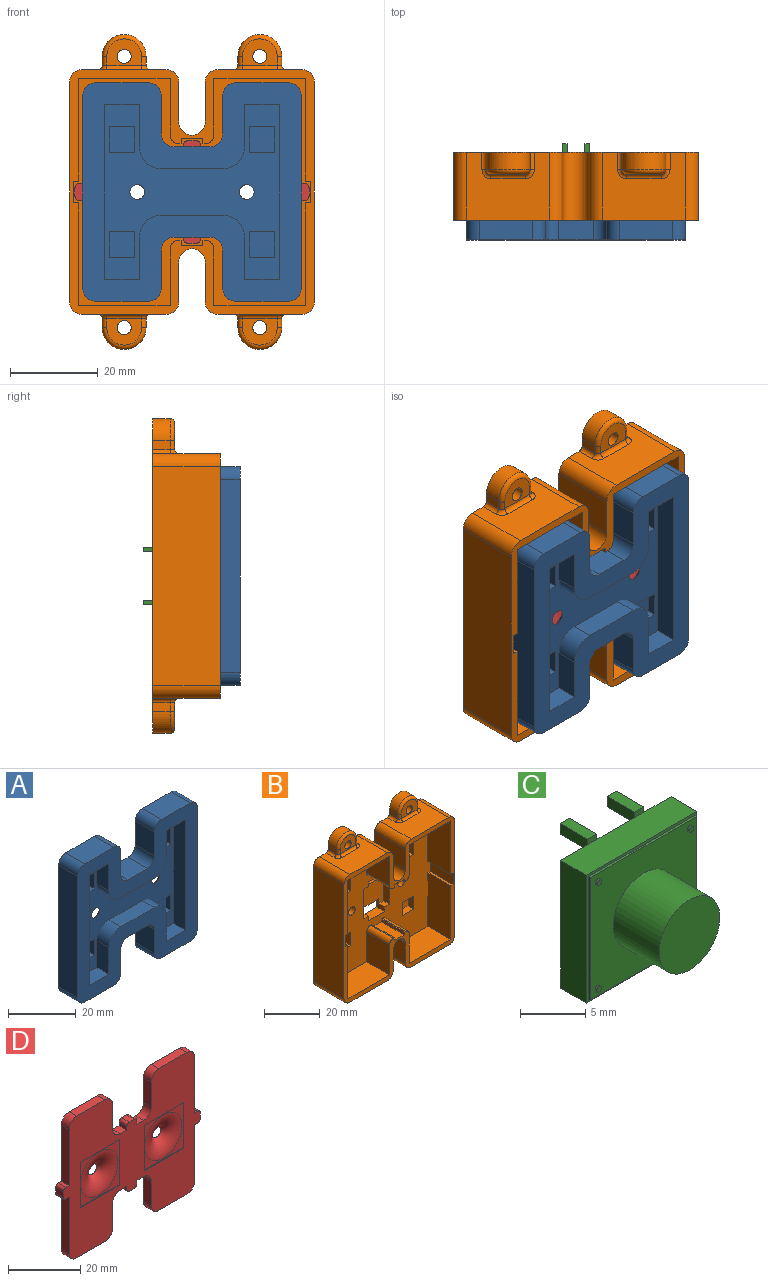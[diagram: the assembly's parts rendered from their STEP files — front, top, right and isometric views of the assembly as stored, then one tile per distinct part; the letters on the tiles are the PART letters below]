
ASSEMBLY  parts=4 mates=3
PART A: 75 faces, bbox 50x8x50 mm
  f0: plane 40x40mm, normal (0,-1,0), area 763.1mm2, adj f14,f15,f16,f17,f18,f19,f20,f21
  f1: plane 50x50mm, normal (0,1,0), area 1606.4mm2, adj f2,f3,f4,f5,f6,f7,f8,f9
  f2: plane 8x8mm, normal (0,0,-1), area 64mm2, adj f1,f26,f32,f33
  f3: plane 8.7x8mm, normal (-1,0,0), area 69.6mm2, adj f1,f26,f33,f34
  f4: plane 12x8mm, normal (0,0,-1), area 96mm2, adj f1,f26,f34,f35
  f5: plane 44x8mm, normal (1,0,0), area 352mm2, adj f1,f26,f35,f36
  f6: plane 12x8mm, normal (0,0,1), area 96mm2, adj f1,f26,f36,f37
  f7: plane 8.7x8mm, normal (-1,0,0), area 69.6mm2, adj f1,f26,f37,f38
  f8: plane 8x8mm, normal (0,0,1), area 64mm2, adj f1,f26,f27,f38
  f9: plane 8.7x8mm, normal (1,0,0), area 69.6mm2, adj f1,f26,f27,f28
  f10: plane 12x8mm, normal (0,0,1), area 96mm2, adj f1,f26,f28,f29
  f11: plane 44x8mm, normal (-1,0,0), area 352mm2, adj f1,f26,f29,f30
  f12: plane 12x8mm, normal (0,0,-1), area 96mm2, adj f1,f26,f30,f31
  f13: plane 8.7x8mm, normal (1,0,0), area 69.6mm2, adj f1,f26,f31,f32
  f14: plane 40x5mm, normal (1,0,0), area 200mm2, adj f0,f15,f25,f26
  f15: plane 8x5mm, normal (0,0,-1), area 40mm2, adj f0,f14,f16,f26
  f16: plane 9.7x5mm, normal (-1,0,0), area 48.5mm2, adj f0,f15,f26,f49
  f17: plane 14x5mm, normal (0,0,-1), area 70mm2, adj f0,f26,f49,f50
  f18: plane 9.7x5mm, normal (1,0,0), area 48.5mm2, adj f0,f19,f26,f50
  f19: plane 8x5mm, normal (0,0,-1), area 40mm2, adj f0,f18,f20,f26
  f20: plane 40x5mm, normal (-1,0,0), area 200mm2, adj f0,f19,f21,f26
  f21: plane 8x5mm, normal (0,0,1), area 40mm2, adj f0,f20,f22,f26
  f22: plane 9.7x5mm, normal (1,0,0), area 48.5mm2, adj f0,f21,f26,f51
  f23: plane 14x5mm, normal (0,0,1), area 70mm2, adj f0,f26,f51,f52
  f24: plane 9.7x5mm, normal (-1,0,0), area 48.5mm2, adj f0,f25,f26,f52
  f25: plane 8x5mm, normal (0,0,1), area 40mm2, adj f0,f14,f24,f26
  f26: plane 50x50mm, normal (0,-1,0), area 1164.8mm2, adj f2,f3,f4,f5,f6,f7,f8,f9
  f27: cylinder r=3mm len=8mm, axis (0,-1,0), area 37.7mm2, adj f1,f8,f9,f26
  f28: cylinder r=3mm len=8mm, axis (0,1,0), area 37.7mm2, adj f1,f9,f10,f26
  f29: cylinder r=3mm len=8mm, axis (0,1,0), area 37.7mm2, adj f1,f10,f11,f26
  f30: cylinder r=3mm len=8mm, axis (0,1,0), area 37.7mm2, adj f1,f11,f12,f26
  f31: cylinder r=3mm len=8mm, axis (0,1,0), area 37.7mm2, adj f1,f12,f13,f26
  f32: cylinder r=3mm len=8mm, axis (0,-1,0), area 37.7mm2, adj f1,f2,f13,f26
  f33: cylinder r=3mm len=8mm, axis (0,-1,0), area 37.7mm2, adj f1,f2,f3,f26
  f34: cylinder r=3mm len=8mm, axis (0,1,0), area 37.7mm2, adj f1,f3,f4,f26
  f35: cylinder r=3mm len=8mm, axis (0,1,0), area 37.7mm2, adj f1,f4,f5,f26
  f36: cylinder r=3mm len=8mm, axis (0,1,0), area 37.7mm2, adj f1,f5,f6,f26
  f37: cylinder r=3mm len=8mm, axis (0,1,0), area 37.7mm2, adj f1,f6,f7,f26
  f38: cylinder r=3mm len=8mm, axis (0,-1,0), area 37.7mm2, adj f1,f7,f8,f26
  f39: plane 15.4x0.1mm, normal (0,0,-1), area 1.5mm2, adj f1,f40,f42,f43
  f40: plane 15.4x0.1mm, normal (-1,0,0), area 1.5mm2, adj f1,f39,f41,f43
  f41: plane 15.4x0.1mm, normal (0,0,1), area 1.5mm2, adj f1,f40,f42,f43
  f42: plane 15.4x0.1mm, normal (1,0,0), area 1.5mm2, adj f1,f39,f41,f43
  f43: plane 15.4x15.4mm, normal (0,1,0), area 66.4mm2, adj f39,f40,f41,f42,f73
  f44: plane 15.4x0.1mm, normal (0,0,-1), area 1.5mm2, adj f1,f45,f47,f48
  f45: plane 15.4x0.1mm, normal (-1,0,0), area 1.5mm2, adj f1,f44,f46,f48
  f46: plane 15.4x0.1mm, normal (0,0,1), area 1.5mm2, adj f1,f45,f47,f48
  f47: plane 15.4x0.1mm, normal (1,0,0), area 1.5mm2, adj f1,f44,f46,f48
  f48: plane 15.4x15.4mm, normal (0,1,0), area 66.4mm2, adj f44,f45,f46,f47,f74
  f49: cylinder r=5mm len=5mm, axis (0,1,0), area 39.3mm2, adj f0,f16,f17,f26
  f50: cylinder r=5mm len=5mm, axis (0,1,0), area 39.3mm2, adj f0,f17,f18,f26
  f51: cylinder r=5mm len=5mm, axis (0,1,0), area 39.3mm2, adj f0,f22,f23,f26
  f52: cylinder r=5mm len=5mm, axis (0,1,0), area 39.3mm2, adj f0,f23,f24,f26
  f53: plane 5.8x2mm, normal (1,0,0), area 11.6mm2, adj f0,f54,f56,f57
  f54: plane 5.8x2mm, normal (0,0,1), area 11.6mm2, adj f0,f53,f55,f57
  f55: plane 5.8x2mm, normal (-1,0,0), area 11.6mm2, adj f0,f54,f56,f57
  f56: plane 5.8x2mm, normal (0,0,-1), area 11.6mm2, adj f0,f53,f55,f57
  f57: plane 5.8x5.8mm, normal (0,-1,0), area 33.6mm2, adj f53,f54,f55,f56
  f58: plane 5.8x2mm, normal (-1,0,0), area 11.6mm2, adj f0,f59,f61,f62
  f59: plane 5.8x2mm, normal (0,0,-1), area 11.6mm2, adj f0,f58,f60,f62
  f60: plane 5.8x2mm, normal (1,0,0), area 11.6mm2, adj f0,f59,f61,f62
  f61: plane 5.8x2mm, normal (0,0,1), area 11.6mm2, adj f0,f58,f60,f62
  f62: plane 5.8x5.8mm, normal (0,-1,0), area 33.6mm2, adj f58,f59,f60,f61
  f63: plane 5.8x2mm, normal (1,0,0), area 11.6mm2, adj f0,f64,f66,f67
  f64: plane 5.8x2mm, normal (0,0,1), area 11.6mm2, adj f0,f63,f65,f67
  f65: plane 5.8x2mm, normal (-1,0,0), area 11.6mm2, adj f0,f64,f66,f67
  f66: plane 5.8x2mm, normal (0,0,-1), area 11.6mm2, adj f0,f63,f65,f67
  f67: plane 5.8x5.8mm, normal (0,-1,0), area 33.6mm2, adj f63,f64,f65,f66
  f68: plane 5.8x2mm, normal (0,0,-1), area 11.6mm2, adj f0,f69,f71,f72
  f69: plane 5.8x2mm, normal (1,0,0), area 11.6mm2, adj f0,f68,f70,f72
  f70: plane 5.8x2mm, normal (0,0,1), area 11.6mm2, adj f0,f69,f71,f72
  f71: plane 5.8x2mm, normal (-1,0,0), area 11.6mm2, adj f0,f68,f70,f72
  f72: plane 5.8x5.8mm, normal (0,-1,0), area 33.6mm2, adj f68,f69,f70,f71
  f73: torus R=7.37mm, axis (0,1,0), area 178.9mm2, adj f0,f43
  f74: torus R=7.37mm, axis (0,1,0), area 178.9mm2, adj f0,f48
PART B: 144 faces, bbox 56x15.5x72.8 mm
  f0: plane 54.4x52mm, normal (0,-1,0), area 2077.7mm2, adj f2,f3,f4,f5,f8,f10,f20,f22
  f1: plane 19x15.5mm, normal (0,0,-1), area 224.2mm2, adj f6,f11,f58,f59,f101,f103,f105,f106
  f2: plane 23.5x11.5mm, normal (1,0,0), area 270.2mm2, adj f0,f6,f35,f55
  f3: plane 11.5x0.5mm, normal (0,0,-1), area 5.8mm2, adj f0,f6,f54,f69
  f4: plane 23.5x11.5mm, normal (-1,0,0), area 270.2mm2, adj f0,f6,f41,f47
  f5: plane 11.5x0.5mm, normal (0,0,1), area 5.8mm2, adj f0,f6,f49,f71
  f6: plane 56x56mm, normal (0,-1,0), area 516.8mm2, adj f1,f2,f3,f4,f5,f12,f13,f14
  f7: plane 8x1mm, normal (0,0,-1), area 8mm2, adj f11,f23,f25,f33
  f8: plane 4x4mm, normal (1,0,0), area 10mm2, adj f0,f9,f11,f26,f32,f33
  f9: plane 8x1mm, normal (0,0,1), area 8mm2, adj f8,f10,f11,f33
  f10: plane 4x4mm, normal (-1,0,0), area 10mm2, adj f0,f9,f11,f26,f31,f33
  f11: plane 72x56mm, normal (0,1,0), area 3112.7mm2, adj f1,f7,f8,f9,f10,f12,f13,f14
  f12: plane 15.5x9mm, normal (-1,0,0), area 139.5mm2, adj f6,f11,f60,f67
  f13: plane 19x15.5mm, normal (0,0,-1), area 224.2mm2, adj f6,f11,f66,f67,f93,f95,f97,f98
  f14: plane 50x15.5mm, normal (1,0,0), area 775mm2, adj f6,f11,f65,f66
  f15: plane 19x15.5mm, normal (0,0,1), area 224.2mm2, adj f6,f11,f64,f65,f108,f110,f112,f114
  f16: plane 15.5x9mm, normal (-1,0,0), area 139.5mm2, adj f6,f11,f62,f64
  f17: plane 15.5x9mm, normal (1,0,0), area 139.5mm2, adj f6,f11,f62,f63
  f18: plane 19x15.5mm, normal (0,0,1), area 224.2mm2, adj f6,f11,f61,f63,f116,f118,f120,f122
  f19: plane 50x15.5mm, normal (-1,0,0), area 775mm2, adj f6,f11,f58,f61
  f20: cylinder r=1.7mm len=4mm, axis (0,1,0), area 42.7mm2, adj f0,f11
  f21: plane 15.5x9mm, normal (1,0,0), area 139.5mm2, adj f6,f11,f59,f60
  f22: cylinder r=1.7mm len=4mm, axis (0,1,0), area 42.7mm2, adj f0,f11
  f23: plane 4x4mm, normal (1,0,0), area 10mm2, adj f0,f7,f11,f24,f28,f33
  f24: plane 8x4mm, normal (0,0,1), area 32mm2, adj f0,f11,f23,f25
  f25: plane 4x4mm, normal (-1,0,0), area 10mm2, adj f0,f7,f11,f24,f29,f33
  f26: plane 8x4mm, normal (0,0,-1), area 32mm2, adj f0,f8,f10,f11
  f27: plane 13x3mm, normal (1,0,0), area 39mm2, adj f0,f28,f32,f33
  f28: plane 3x2.5mm, normal (0,0,1), area 7.5mm2, adj f0,f23,f27,f33
  f29: plane 3x2.5mm, normal (0,0,1), area 7.5mm2, adj f0,f25,f30,f33
  f30: plane 13x3mm, normal (-1,0,0), area 39mm2, adj f0,f29,f31,f33
  f31: plane 3x2.5mm, normal (0,0,-1), area 7.5mm2, adj f0,f10,f30,f33
  f32: plane 3x2.5mm, normal (0,0,-1), area 7.5mm2, adj f0,f8,f27,f33
  f33: plane 13x13mm, normal (0,-1,0), area 137mm2, adj f7,f8,f9,f10,f23,f25,f27,f28
  f34: plane 23.5x11.5mm, normal (1,0,0), area 270.2mm2, adj f0,f6,f45,f57
  f35: plane 21x11.5mm, normal (0,0,-1), area 241.5mm2, adj f0,f2,f6,f36
  f36: plane 13x11.5mm, normal (-1,0,0), area 149.5mm2, adj f0,f6,f35,f68
  f37: plane 11.5x0.5mm, normal (0,0,-1), area 5.8mm2, adj f0,f6,f53,f68
  f38: plane 13x11.5mm, normal (1,0,0), area 149.5mm2, adj f0,f6,f39,f69
  f39: plane 21x11.5mm, normal (0,0,-1), area 241.5mm2, adj f0,f6,f38,f40
  f40: plane 23.5x11.5mm, normal (-1,0,0), area 270.2mm2, adj f0,f6,f39,f46
  f41: plane 21x11.5mm, normal (0,0,1), area 241.5mm2, adj f0,f4,f6,f42
  f42: plane 13x11.5mm, normal (1,0,0), area 149.5mm2, adj f0,f6,f41,f70
  f43: plane 11.5x0.5mm, normal (0,0,1), area 5.8mm2, adj f0,f6,f51,f70
  f44: plane 13x11.5mm, normal (-1,0,0), area 149.5mm2, adj f0,f6,f45,f71
  f45: plane 21x11.5mm, normal (0,0,1), area 241.5mm2, adj f0,f6,f34,f44
  f46: plane 11.5x1.2mm, normal (0,0,-1), area 13.8mm2, adj f0,f6,f40,f48
  f47: plane 11.5x1.2mm, normal (0,0,1), area 13.8mm2, adj f0,f4,f6,f48
  f48: plane 11.5x5mm, normal (-1,0,0), area 57.5mm2, adj f0,f6,f46,f47
  f49: plane 11.5x1.2mm, normal (1,0,0), area 13.8mm2, adj f0,f5,f6,f50
  f50: plane 11.5x5mm, normal (0,0,1), area 57.5mm2, adj f0,f6,f49,f51
  f51: plane 11.5x1.2mm, normal (-1,0,0), area 13.8mm2, adj f0,f6,f43,f50
  f52: plane 11.5x5mm, normal (0,0,-1), area 57.5mm2, adj f0,f6,f53,f54
  f53: plane 11.5x1.2mm, normal (1,0,0), area 13.8mm2, adj f0,f6,f37,f52
  f54: plane 11.5x1.2mm, normal (-1,0,0), area 13.8mm2, adj f0,f3,f6,f52
  f55: plane 11.5x1.2mm, normal (0,0,-1), area 13.8mm2, adj f0,f2,f6,f56
  f56: plane 11.5x5mm, normal (1,0,0), area 57.5mm2, adj f0,f6,f55,f57
  f57: plane 11.5x1.2mm, normal (0,0,1), area 13.8mm2, adj f0,f6,f34,f56
  f58: cylinder r=3mm len=15.5mm, axis (0,1,0), area 73mm2, adj f1,f6,f11,f19
  f59: cylinder r=3mm len=15.5mm, axis (0,1,0), area 73mm2, adj f1,f6,f11,f21
  f60: cylinder r=3mm len=15.5mm, axis (0,1,0), area 146.1mm2, adj f6,f11,f12,f21
  f61: cylinder r=3mm len=15.5mm, axis (0,-1,0), area 73mm2, adj f6,f11,f18,f19
  f62: cylinder r=3mm len=15.5mm, axis (0,-1,0), area 146.1mm2, adj f6,f11,f16,f17
  f63: cylinder r=3mm len=15.5mm, axis (0,1,0), area 73mm2, adj f6,f11,f17,f18
  f64: cylinder r=3mm len=15.5mm, axis (0,1,0), area 73mm2, adj f6,f11,f15,f16
  f65: cylinder r=3mm len=15.5mm, axis (0,1,0), area 73mm2, adj f6,f11,f14,f15
  f66: cylinder r=3mm len=15.5mm, axis (0,1,0), area 73mm2, adj f6,f11,f13,f14
  f67: cylinder r=3mm len=15.5mm, axis (0,1,0), area 73mm2, adj f6,f11,f12,f13
  f68: cylinder r=2mm len=11.5mm, axis (0,1,0), area 36.1mm2, adj f0,f6,f36,f37
  f69: cylinder r=2mm len=11.5mm, axis (0,1,0), area 36.1mm2, adj f0,f3,f6,f38
  f70: cylinder r=2mm len=11.5mm, axis (0,1,0), area 36.1mm2, adj f0,f6,f42,f43
  f71: cylinder r=2mm len=11.5mm, axis (0,1,0), area 36.1mm2, adj f0,f5,f6,f44
  f72: plane 4x2mm, normal (-1,0,0), area 8mm2, adj f11,f73,f100,f101
  f73: cylinder r=5mm len=10mm, axis (0,1,0), area 62.8mm2, adj f11,f72,f74,f102
  f74: plane 4x2mm, normal (1,0,0), area 8mm2, adj f11,f73,f104,f107
  f75: cylinder r=1.6mm len=5mm, axis (0,1,0), area 50.3mm2, adj f11,f76
  f76: plane 8x6mm, normal (0,-1,0), area 33.1mm2, adj f75,f100,f102,f104,f105
  f77: plane 4x2mm, normal (-1,0,0), area 8mm2, adj f11,f80,f116,f117
  f78: plane 4x2mm, normal (1,0,0), area 8mm2, adj f11,f80,f121,f123
  f79: cylinder r=1.6mm len=5mm, axis (0,1,0), area 50.3mm2, adj f11,f81
  f80: cylinder r=5mm len=10mm, axis (0,1,0), area 62.8mm2, adj f11,f77,f78,f119
  f81: plane 8x6mm, normal (0,-1,0), area 33.1mm2, adj f79,f117,f119,f120,f121
  f82: plane 4x2mm, normal (-1,0,0), area 8mm2, adj f11,f85,f108,f109
  f83: plane 4x2mm, normal (1,0,0), area 8mm2, adj f11,f85,f113,f115
  f84: cylinder r=1.6mm len=5mm, axis (0,1,0), area 50.3mm2, adj f11,f86
  f85: cylinder r=5mm len=10mm, axis (0,1,0), area 62.8mm2, adj f11,f82,f83,f111
  f86: plane 8x6mm, normal (0,-1,0), area 33.1mm2, adj f84,f109,f111,f112,f113
  f87: plane 4x2mm, normal (1,0,0), area 8mm2, adj f11,f90,f96,f99
  f88: plane 4x2mm, normal (-1,0,0), area 8mm2, adj f11,f90,f92,f93
  f89: cylinder r=1.6mm len=5mm, axis (0,1,0), area 50.3mm2, adj f11,f91
  f90: cylinder r=5mm len=10mm, axis (0,1,0), area 62.8mm2, adj f11,f87,f88,f94
  f91: plane 8x6mm, normal (0,-1,0), area 33.1mm2, adj f89,f92,f94,f96,f97
  f92: cylinder r=1mm len=2mm, axis (0,0,1), area 3.1mm2, adj f88,f91,f94,f95
  f93: cylinder r=1mm len=4mm, axis (0,-1,0), area 6.3mm2, adj f11,f13,f88,f95
  f94: torus R=4mm, axis (0,-1,0), area 22.9mm2, adj f90,f91,f92,f96
  f95: torus R=2mm, axis (0,0,-1), area 3.4mm2, adj f13,f92,f93,f97
  f96: cylinder r=1mm len=2mm, axis (0,0,-1), area 3.1mm2, adj f87,f91,f94,f98
  f97: cylinder r=1mm len=8mm, axis (1,0,0), area 12.6mm2, adj f13,f91,f95,f98
  f98: torus R=2mm, axis (0,0,-1), area 3.4mm2, adj f13,f96,f97,f99
  f99: cylinder r=1mm len=4mm, axis (0,1,0), area 6.3mm2, adj f11,f13,f87,f98
  f100: cylinder r=1mm len=2mm, axis (0,0,1), area 3.1mm2, adj f72,f76,f102,f103
  f101: cylinder r=1mm len=4mm, axis (0,1,0), area 6.3mm2, adj f1,f11,f72,f103
  f102: torus R=4mm, axis (0,-1,0), area 22.9mm2, adj f73,f76,f100,f104
  f103: torus R=2mm, axis (0,0,1), area 3.4mm2, adj f1,f100,f101,f105
  f104: cylinder r=1mm len=2mm, axis (0,0,-1), area 3.1mm2, adj f74,f76,f102,f106
  f105: cylinder r=1mm len=8mm, axis (1,0,0), area 12.6mm2, adj f1,f76,f103,f106
  f106: torus R=2mm, axis (0,0,1), area 3.4mm2, adj f1,f104,f105,f107
  f107: cylinder r=1mm len=4mm, axis (0,-1,0), area 6.3mm2, adj f1,f11,f74,f106
  f108: cylinder r=1mm len=4mm, axis (0,1,0), area 6.3mm2, adj f11,f15,f82,f110
  f109: cylinder r=1mm len=2mm, axis (0,0,1), area 3.1mm2, adj f82,f86,f110,f111
  f110: torus R=2mm, axis (0,0,1), area 3.4mm2, adj f15,f108,f109,f112
  f111: torus R=4mm, axis (0,-1,0), area 22.9mm2, adj f85,f86,f109,f113
  f112: cylinder r=1mm len=8mm, axis (-1,0,0), area 12.6mm2, adj f15,f86,f110,f114
  f113: cylinder r=1mm len=2mm, axis (0,0,-1), area 3.1mm2, adj f83,f86,f111,f114
  f114: torus R=2mm, axis (0,0,1), area 3.4mm2, adj f15,f112,f113,f115
  f115: cylinder r=1mm len=4mm, axis (0,-1,0), area 6.3mm2, adj f11,f15,f83,f114
  f116: cylinder r=1mm len=4mm, axis (0,1,0), area 6.3mm2, adj f11,f18,f77,f118
  f117: cylinder r=1mm len=2mm, axis (0,0,1), area 3.1mm2, adj f77,f81,f118,f119
  f118: torus R=2mm, axis (0,0,1), area 3.4mm2, adj f18,f116,f117,f120
  f119: torus R=4mm, axis (0,-1,0), area 22.9mm2, adj f80,f81,f117,f121
  f120: cylinder r=1mm len=8mm, axis (-1,0,0), area 12.6mm2, adj f18,f81,f118,f122
  f121: cylinder r=1mm len=2mm, axis (0,0,-1), area 3.1mm2, adj f78,f81,f119,f122
  f122: torus R=2mm, axis (0,0,1), area 3.4mm2, adj f18,f120,f121,f123
  f123: cylinder r=1mm len=4mm, axis (0,-1,0), area 6.3mm2, adj f11,f18,f78,f122
  f124: plane 5.8x3mm, normal (0,0,-1), area 17.4mm2, adj f0,f125,f127,f128
  f125: plane 5.8x3mm, normal (1,0,0), area 17.4mm2, adj f0,f124,f126,f128
  f126: plane 5.8x3mm, normal (0,0,1), area 17.4mm2, adj f0,f125,f127,f128
  f127: plane 5.8x3mm, normal (-1,0,0), area 17.4mm2, adj f0,f124,f126,f128
  f128: plane 5.8x5.8mm, normal (0,-1,0), area 33.6mm2, adj f124,f125,f126,f127
  f129: plane 5.8x3mm, normal (0,0,1), area 17.4mm2, adj f0,f130,f132,f133
  f130: plane 5.8x3mm, normal (-1,0,0), area 17.4mm2, adj f0,f129,f131,f133
  f131: plane 5.8x3mm, normal (0,0,-1), area 17.4mm2, adj f0,f130,f132,f133
  f132: plane 5.8x3mm, normal (1,0,0), area 17.4mm2, adj f0,f129,f131,f133
  f133: plane 5.8x5.8mm, normal (0,-1,0), area 33.6mm2, adj f129,f130,f131,f132
  f134: plane 5.8x3mm, normal (1,0,0), area 17.4mm2, adj f0,f135,f137,f138
  f135: plane 5.8x3mm, normal (0,0,1), area 17.4mm2, adj f0,f134,f136,f138
  f136: plane 5.8x3mm, normal (-1,0,0), area 17.4mm2, adj f0,f135,f137,f138
  f137: plane 5.8x3mm, normal (0,0,-1), area 17.4mm2, adj f0,f134,f136,f138
  f138: plane 5.8x5.8mm, normal (0,-1,0), area 33.6mm2, adj f134,f135,f136,f137
  f139: plane 5.8x3mm, normal (-1,0,0), area 17.4mm2, adj f0,f140,f142,f143
  f140: plane 5.8x3mm, normal (0,0,-1), area 17.4mm2, adj f0,f139,f141,f143
  f141: plane 5.8x3mm, normal (1,0,0), area 17.4mm2, adj f0,f140,f142,f143
  f142: plane 5.8x3mm, normal (0,0,1), area 17.4mm2, adj f0,f139,f141,f143
  f143: plane 5.8x5.8mm, normal (0,-1,0), area 33.6mm2, adj f139,f140,f141,f142
PART C: 45 faces, bbox 12x11x13 mm
  f0: plane 12x12mm, normal (0,1,0), area 142mm2, adj f17,f18,f19,f20,f22,f23,f24,f27
  f1: plane 11.5x11.5mm, normal (0,-1,0), area 97.3mm2, adj f2,f4,f6,f8,f10,f12,f13,f14
  f2: cylinder r=3.3mm len=6.6mm, axis (0,1,0), area 103.7mm2, adj f1,f3
  f3: plane 6.6x6.6mm, normal (0,-1,0), area 34.2mm2, adj f2
  f4: cylinder r=0.25mm len=0.5mm, axis (0,1,0), area 0.3mm2, adj f1,f5
  f5: plane 0.5x0.5mm, normal (0,-1,0), area 0.2mm2, adj f4
  f6: cylinder r=0.25mm len=0.5mm, axis (0,1,0), area 0.3mm2, adj f1,f7
  f7: plane 0.5x0.5mm, normal (0,-1,0), area 0.2mm2, adj f6
  f8: cylinder r=0.25mm len=0.5mm, axis (0,1,0), area 0.3mm2, adj f1,f9
  f9: plane 0.5x0.5mm, normal (0,-1,0), area 0.2mm2, adj f8
  f10: cylinder r=0.25mm len=0.5mm, axis (0,1,0), area 0.3mm2, adj f1,f11
  f11: plane 0.5x0.5mm, normal (0,-1,0), area 0.2mm2, adj f10
  f12: plane 11.5x0.2mm, normal (-1,0,0), area 2.3mm2, adj f1,f13,f15,f16
  f13: plane 11.5x0.2mm, normal (0,0,1), area 2.3mm2, adj f1,f12,f14,f16
  f14: plane 11.5x0.2mm, normal (1,0,0), area 2.3mm2, adj f1,f13,f15,f16
  f15: plane 11.5x0.2mm, normal (0,0,-1), area 2.3mm2, adj f1,f12,f14,f16
  f16: plane 12x12mm, normal (0,-1,0), area 11.8mm2, adj f12,f13,f14,f15,f17,f18,f19,f20
  f17: plane 12x2.8mm, normal (-1,0,0), area 33.6mm2, adj f0,f16,f18,f20
  f18: plane 12x2.8mm, normal (0,0,1), area 33.6mm2, adj f0,f16,f17,f19,f26,f32
  f19: plane 12x2.8mm, normal (1,0,0), area 33.6mm2, adj f0,f16,f18,f20
  f20: plane 12x2.8mm, normal (0,0,-1), area 33.6mm2, adj f0,f16,f17,f19,f33,f39
  f21: plane 3x1mm, normal (0,0,1), area 3mm2, adj f22,f24,f25,f26
  f22: plane 3x1mm, normal (1,0,0), area 3mm2, adj f0,f21,f23,f25,f26
  f23: plane 3x1mm, normal (0,0,-1), area 3mm2, adj f0,f22,f24,f25
  f24: plane 3x1mm, normal (-1,0,0), area 3mm2, adj f0,f21,f23,f25,f26
  f25: plane 1x1mm, normal (0,1,0), area 1mm2, adj f21,f22,f23,f24
  f26: plane 1x0.5mm, normal (0,-1,0), area 0.5mm2, adj f18,f21,f22,f24
  f27: plane 3x1mm, normal (0,0,-1), area 3mm2, adj f0,f28,f30,f31
  f28: plane 3x1mm, normal (-1,0,0), area 3mm2, adj f0,f27,f29,f31,f32
  f29: plane 3x1mm, normal (0,0,1), area 3mm2, adj f28,f30,f31,f32
  f30: plane 3x1mm, normal (1,0,0), area 3mm2, adj f0,f27,f29,f31,f32
  f31: plane 1x1mm, normal (0,1,0), area 1mm2, adj f27,f28,f29,f30
  f32: plane 1x0.5mm, normal (0,-1,0), area 0.5mm2, adj f18,f28,f29,f30
  f33: plane 1x0.5mm, normal (0,-1,0), area 0.5mm2, adj f20,f34,f35,f36
  f34: plane 3x1mm, normal (1,0,0), area 3mm2, adj f0,f33,f35,f37,f38
  f35: plane 3x1mm, normal (0,0,-1), area 3mm2, adj f33,f34,f36,f38
  f36: plane 3x1mm, normal (-1,0,0), area 3mm2, adj f0,f33,f35,f37,f38
  f37: plane 3x1mm, normal (0,0,1), area 3mm2, adj f0,f34,f36,f38
  f38: plane 1x1mm, normal (0,1,0), area 1mm2, adj f34,f35,f36,f37
  f39: plane 1x0.5mm, normal (0,-1,0), area 0.5mm2, adj f20,f40,f41,f42
  f40: plane 3x1mm, normal (1,0,0), area 3mm2, adj f0,f39,f41,f43,f44
  f41: plane 3x1mm, normal (0,0,-1), area 3mm2, adj f39,f40,f42,f44
  f42: plane 3x1mm, normal (-1,0,0), area 3mm2, adj f0,f39,f41,f43,f44
  f43: plane 3x1mm, normal (0,0,1), area 3mm2, adj f0,f40,f42,f44
  f44: plane 1x1mm, normal (0,1,0), area 1mm2, adj f40,f41,f42,f43
PART D: 82 faces, bbox 53.5x7.2x48 mm
  f0: plane 53.5x48mm, normal (0,-1,0), area 1470.3mm2, adj f2,f3,f4,f5,f6,f7,f8,f9
  f1: plane 53.5x48mm, normal (0,1,0), area 1791.9mm2, adj f2,f3,f4,f5,f6,f7,f8,f9
  f2: plane 3x2.55mm, normal (0,0,-1), area 7.7mm2, adj f0,f1,f3,f35
  f3: plane 3x1.2mm, normal (-1,0,0), area 3.6mm2, adj f0,f1,f2,f76
  f4: plane 3x2mm, normal (0,0,-1), area 6mm2, adj f0,f1,f76,f77
  f5: plane 3x1.2mm, normal (1,0,0), area 3.6mm2, adj f0,f1,f6,f77
  f6: plane 3x2.55mm, normal (0,0,-1), area 7.6mm2, adj f0,f1,f5,f36
  f7: plane 8.5x3mm, normal (-1,0,0), area 25.5mm2, adj f0,f1,f36,f37
  f8: plane 11x3mm, normal (0,0,-1), area 33mm2, adj f0,f1,f37,f38
  f9: plane 19x3mm, normal (1,0,0), area 57mm2, adj f0,f1,f10,f38
  f10: plane 3x1.2mm, normal (0,0,-1), area 3.6mm2, adj f0,f1,f9,f74
  f11: plane 3x2mm, normal (1,0,0), area 6mm2, adj f0,f1,f74,f75
  f12: plane 3x1.2mm, normal (0,0,1), area 3.6mm2, adj f0,f1,f13,f75
  f13: plane 19x3mm, normal (1,0,0), area 57mm2, adj f0,f1,f12,f39
  f14: plane 11x3mm, normal (0,0,1), area 33mm2, adj f0,f1,f39,f40
  f15: plane 8.5x3mm, normal (-1,0,0), area 25.5mm2, adj f0,f1,f40,f41
  f16: plane 3x2.55mm, normal (0,0,1), area 7.6mm2, adj f0,f1,f17,f41
  f17: plane 3x1.2mm, normal (1,0,0), area 3.6mm2, adj f0,f1,f16,f80
  f18: plane 3x2mm, normal (0,0,1), area 6mm2, adj f0,f1,f80,f81
  f19: plane 3x1.2mm, normal (-1,0,0), area 3.6mm2, adj f0,f1,f20,f81
  f20: plane 3x2.55mm, normal (0,0,1), area 7.7mm2, adj f0,f1,f19,f30
  f21: plane 8.5x3mm, normal (1,0,0), area 25.5mm2, adj f0,f1,f30,f31
  f22: plane 11x3mm, normal (0,0,1), area 33mm2, adj f0,f1,f31,f32
  f23: plane 19x3mm, normal (-1,0,0), area 57mm2, adj f0,f1,f24,f32
  f24: plane 3x1.2mm, normal (0,0,1), area 3.6mm2, adj f0,f1,f23,f78
  f25: plane 3x2mm, normal (-1,0,0), area 6mm2, adj f0,f1,f78,f79
  f26: plane 3x1.2mm, normal (0,0,-1), area 3.6mm2, adj f0,f1,f27,f79
  f27: plane 19x3mm, normal (-1,0,0), area 57mm2, adj f0,f1,f26,f33
  f28: plane 11x3mm, normal (0,0,-1), area 33mm2, adj f0,f1,f33,f34
  f29: plane 8.5x3mm, normal (1,0,0), area 25.5mm2, adj f0,f1,f34,f35
  f30: cylinder r=3mm len=3mm, axis (0,-1,0), area 14.1mm2, adj f0,f1,f20,f21
  f31: cylinder r=3mm len=3mm, axis (0,1,0), area 14.1mm2, adj f0,f1,f21,f22
  f32: cylinder r=3mm len=3mm, axis (0,1,0), area 14.1mm2, adj f0,f1,f22,f23
  f33: cylinder r=3mm len=3mm, axis (0,1,0), area 14.1mm2, adj f0,f1,f27,f28
  f34: cylinder r=3mm len=3mm, axis (0,1,0), area 14.1mm2, adj f0,f1,f28,f29
  f35: cylinder r=3mm len=3mm, axis (0,-1,0), area 14.1mm2, adj f0,f1,f2,f29
  f36: cylinder r=3mm len=3mm, axis (0,-1,0), area 14.1mm2, adj f0,f1,f6,f7
  f37: cylinder r=3mm len=3mm, axis (0,1,0), area 14.1mm2, adj f0,f1,f7,f8
  f38: cylinder r=3mm len=3mm, axis (0,1,0), area 14.1mm2, adj f0,f1,f8,f9
  f39: cylinder r=3mm len=3mm, axis (0,1,0), area 14.1mm2, adj f0,f1,f13,f14
  f40: cylinder r=3mm len=3mm, axis (0,1,0), area 14.1mm2, adj f0,f1,f14,f15
  f41: cylinder r=3mm len=3mm, axis (0,-1,0), area 14.1mm2, adj f0,f1,f15,f16
  f42: plane 5.8x2mm, normal (0,0,-1), area 11.6mm2, adj f1,f43,f45,f46
  f43: plane 5.8x2mm, normal (-1,0,0), area 11.6mm2, adj f1,f42,f44,f46
  f44: plane 5.8x2mm, normal (0,0,1), area 11.6mm2, adj f1,f43,f45,f46
  f45: plane 5.8x2mm, normal (1,0,0), area 11.6mm2, adj f1,f42,f44,f46
  f46: plane 5.8x5.8mm, normal (0,1,0), area 33.6mm2, adj f42,f43,f44,f45
  f47: plane 5.8x2mm, normal (0,0,1), area 11.6mm2, adj f1,f48,f50,f51
  f48: plane 5.8x2mm, normal (1,0,0), area 11.6mm2, adj f1,f47,f49,f51
  f49: plane 5.8x2mm, normal (0,0,-1), area 11.6mm2, adj f1,f48,f50,f51
  f50: plane 5.8x2mm, normal (-1,0,0), area 11.6mm2, adj f1,f47,f49,f51
  f51: plane 5.8x5.8mm, normal (0,1,0), area 33.6mm2, adj f47,f48,f49,f50
  f52: plane 5.8x2mm, normal (0,0,1), area 11.6mm2, adj f1,f53,f55,f56
  f53: plane 5.8x2mm, normal (1,0,0), area 11.6mm2, adj f1,f52,f54,f56
  f54: plane 5.8x2mm, normal (0,0,-1), area 11.6mm2, adj f1,f53,f55,f56
  f55: plane 5.8x2mm, normal (-1,0,0), area 11.6mm2, adj f1,f52,f54,f56
  f56: plane 5.8x5.8mm, normal (0,1,0), area 33.6mm2, adj f52,f53,f54,f55
  f57: plane 5.8x2mm, normal (-1,0,0), area 11.6mm2, adj f1,f58,f60,f61
  f58: plane 5.8x2mm, normal (0,0,1), area 11.6mm2, adj f1,f57,f59,f61
  f59: plane 5.8x2mm, normal (1,0,0), area 11.6mm2, adj f1,f58,f60,f61
  f60: plane 5.8x2mm, normal (0,0,-1), area 11.6mm2, adj f1,f57,f59,f61
  f61: plane 5.8x5.8mm, normal (0,1,0), area 33.6mm2, adj f57,f58,f59,f60
  f62: plane 15.4x0.2mm, normal (0,0,-1), area 3.1mm2, adj f0,f63,f65,f66
  f63: plane 15.4x0.2mm, normal (1,0,0), area 3.1mm2, adj f0,f62,f64,f66
  f64: plane 15.4x0.2mm, normal (0,0,1), area 3.1mm2, adj f0,f63,f65,f66
  f65: plane 15.4x0.2mm, normal (-1,0,0), area 3.1mm2, adj f0,f62,f64,f66
  f66: plane 15.4x15.4mm, normal (0,-1,0), area 69.7mm2, adj f62,f63,f64,f65,f73
  f67: plane 15.4x0.2mm, normal (0,0,-1), area 3.1mm2, adj f0,f68,f70,f71
  f68: plane 15.4x0.2mm, normal (1,0,0), area 3.1mm2, adj f0,f67,f69,f71
  f69: plane 15.4x0.2mm, normal (0,0,1), area 3.1mm2, adj f0,f68,f70,f71
  f70: plane 15.4x0.2mm, normal (-1,0,0), area 3.1mm2, adj f0,f67,f69,f71
  f71: plane 15.4x15.4mm, normal (0,-1,0), area 69.7mm2, adj f67,f68,f69,f70,f72
  f72: torus R=7.3mm, axis (0,-1,0), area 174.6mm2, adj f1,f71
  f73: torus R=7.3mm, axis (0,-1,0), area 174.6mm2, adj f1,f66
  f74: cylinder r=1mm len=3mm, axis (0,1,0), area 4.7mm2, adj f0,f1,f10,f11
  f75: cylinder r=1mm len=3mm, axis (0,-1,0), area 4.7mm2, adj f0,f1,f11,f12
  f76: cylinder r=1mm len=3mm, axis (0,1,0), area 4.7mm2, adj f0,f1,f3,f4
  f77: cylinder r=1mm len=3mm, axis (0,-1,0), area 4.7mm2, adj f0,f1,f4,f5
  f78: cylinder r=1mm len=3mm, axis (0,-1,0), area 4.7mm2, adj f0,f1,f24,f25
  f79: cylinder r=1mm len=3mm, axis (0,1,0), area 4.7mm2, adj f0,f1,f25,f26
  f80: cylinder r=1mm len=3mm, axis (0,1,0), area 4.7mm2, adj f0,f1,f17,f18
  f81: cylinder r=1mm len=3mm, axis (0,-1,0), area 4.7mm2, adj f0,f1,f18,f19
PLACE A t=(-69.4,-30.21,3)mm
PLACE B t=(-55.56,-18.21,32.09)mm
PLACE C t=(-91.73,-19.21,13.42)mm
PLACE D t=(-88.84,-27.21,13.2)mm
MATE fastened C.f2 <-> D.f1  axis (0,-1,0) through (-80.61,-27.21,25.99)mm
MATE fastened D.f0 <-> A.f1  axis (0,-1,0) through (-80.61,-30.21,25.99)mm
MATE fastened B.f33 <-> C.f2  axis (0,-1,0) through (-80.61,-19.21,25.99)mm
